# Revit family: Showerhead-American_Standard-Flowise-1660.641
name_source: partatom
category: Plumbing Fixtures
revit_build: Autodesk Revit 2014 (Build: 20130308_1515(x64)
units: mm (PartAtom-declared; Revit-internal decimal feet)

## types (1)
- 1660.144
    Assembly Code = D2010700
    CW Connection = No
    CWFU = 3
    Default Elevation = 0"
    Description = 1660.144 Water Saving 3-Function Hand Shower
    Finish = Brass-American Standard-002-Polished Chrome
    Flow Rate = 2.0gpm/ 7.6L/min.
    HW Connection = No
    HWFU = 3
    Height = 9 1/2"
    Manufacturer = American Standard
    Material = Brass-American Standard-002-Polished Chrome
    Model = 1660.144
    NPT Connection Size = 3/4"
    Price = Prices may vary. Please consult Manufacturer Representative for most up-to-date price list.
    Product Documentation Link = https://www.americanstandard-us.com
    Product Page URL = https://www.americanstandard-us.com
    Specification = Hand Shower shall have at least 3 spray patterns. Hand Shower shall have a pressure compensating flow control device.
Hand Shower shall include check valve to prevent cross flow of hot and cold water.
    URL = https://www.americanstandard-us.com
    Vent Connection = No
    WFU = 4
    Waste Connection = No
    Width = 3 7/8"

## geometry (parser evidence)
native form markers: Sweep x1
no freeform markers — native parametric forms only
